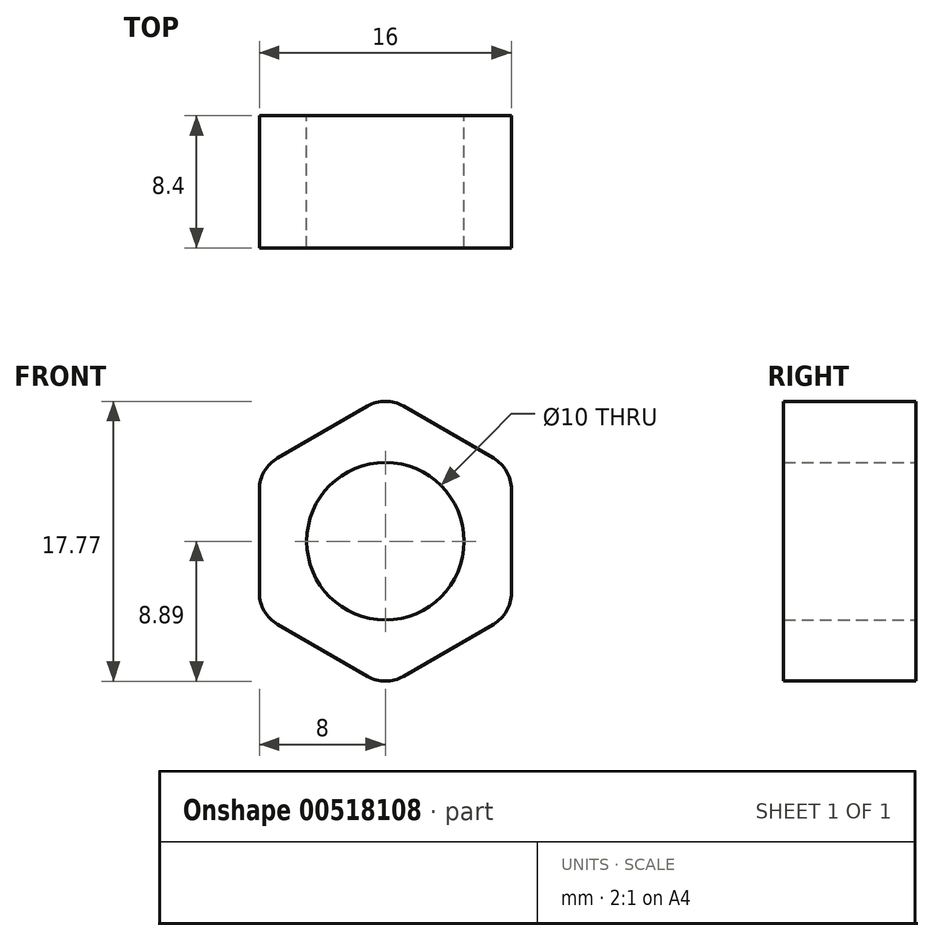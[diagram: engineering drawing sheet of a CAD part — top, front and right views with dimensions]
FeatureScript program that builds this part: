
annotation { "Feature Type Name" : "Feature", "Feature Type Description" : "" }
export const myFeature = defineFeature(function(context is Context, id is Id, definition is map)
    precondition{}
    {
        {
            assignVariable(context, id + "F0", {"name" : "m", "anyValue" : 8.4});
        }
        {
            var Q0;
            Q0=qCreatedBy(makeId("Front.planeOp"),FACE);
            var sketch = newSketch(context, id + "F1", { "sketchPlane" : qUnion([Q0])});
            skLineSegment(sketch, "E0", {"start": v(-1.14, 8.58) * mm, "end": v(-6.86, 5.28) * mm});
            skLineSegment(sketch, "E1", {"start": v(-8, 3.3) * mm, "end": v(-8, -3.3) * mm});
            skLineSegment(sketch, "E2", {"start": v(-6.86, -5.28) * mm, "end": v(-1.14, -8.58) * mm});
            skLineSegment(sketch, "E3", {"start": v(1.14, -8.58) * mm, "end": v(6.86, -5.28) * mm});
            skLineSegment(sketch, "E4", {"start": v(8, -3.3) * mm, "end": v(8, 3.3) * mm});
            skLineSegment(sketch, "E5", {"start": v(6.86, 5.28) * mm, "end": v(1.14, 8.58) * mm});
            skCircle(sketch, "E6", {"center": v(0, 0) * mm, "radius": 5 * mm});
            skLineSegment(sketch, "E7", {"start": v(0, 9.24) * mm, "end": v(0, -9.24) * mm, "construction": true});
            skLineSegment(sketch, "E8", {"start": v(-8, 0) * mm, "end": v(8, 0) * mm, "construction": true});
            skPoint(sketch, "E9.visualSharp", {"position": v(0, 9.24) * mm});
            skArc(sketch, "E9.filletArc", {"start": v(1.14, 8.58) * mm, "mid": v(0, 8.88) * mm, "end": v(-1.14, 8.58) * mm});
            skPoint(sketch, "E10.visualSharp", {"position": v(8, 4.62) * mm});
            skArc(sketch, "E10.filletArc", {"start": v(8, 3.3) * mm, "mid": v(7.7, 4.44) * mm, "end": v(6.86, 5.28) * mm});
            skPoint(sketch, "E11.visualSharp", {"position": v(8, -4.62) * mm});
            skArc(sketch, "E11.filletArc", {"start": v(6.86, -5.28) * mm, "mid": v(7.7, -4.44) * mm, "end": v(8, -3.3) * mm});
            skPoint(sketch, "E12.visualSharp", {"position": v(0, -9.24) * mm});
            skArc(sketch, "E12.filletArc", {"start": v(-1.14, -8.58) * mm, "mid": v(0, -8.88) * mm, "end": v(1.14, -8.58) * mm});
            skPoint(sketch, "E13.visualSharp", {"position": v(-8, -4.62) * mm});
            skArc(sketch, "E13.filletArc", {"start": v(-8, -3.3) * mm, "mid": v(-7.7, -4.44) * mm, "end": v(-6.86, -5.28) * mm});
            skPoint(sketch, "E14.visualSharp", {"position": v(-8, 4.62) * mm});
            skArc(sketch, "E14.filletArc", {"start": v(-6.86, 5.28) * mm, "mid": v(-7.7, 4.44) * mm, "end": v(-8, 3.3) * mm});
            skLineSegment(sketch, "E15", {"start": v(4, 6.93) * mm, "end": v(-4, -6.93) * mm, "construction": true});
            skSolve(sketch);
        }
        {
            var Q0;
            Q0=makeQuery(id+"F1.imprint","IMPRINT",FACE,{"disambiguationData":[TD([[makeQuery(id+"F1.imprint","IMPRINT",EDGE,{"derivedFrom":sQuery(id+"F1.wireOp",EDGE,"E0")}),1.0]])]});
            extrude(context, id + "F2", {"entities" : qUnion([Q0]), "depth" : (getVariable(context, 'm')) * mm, "offsetDistance" : 25 * mm});
        }
    });
